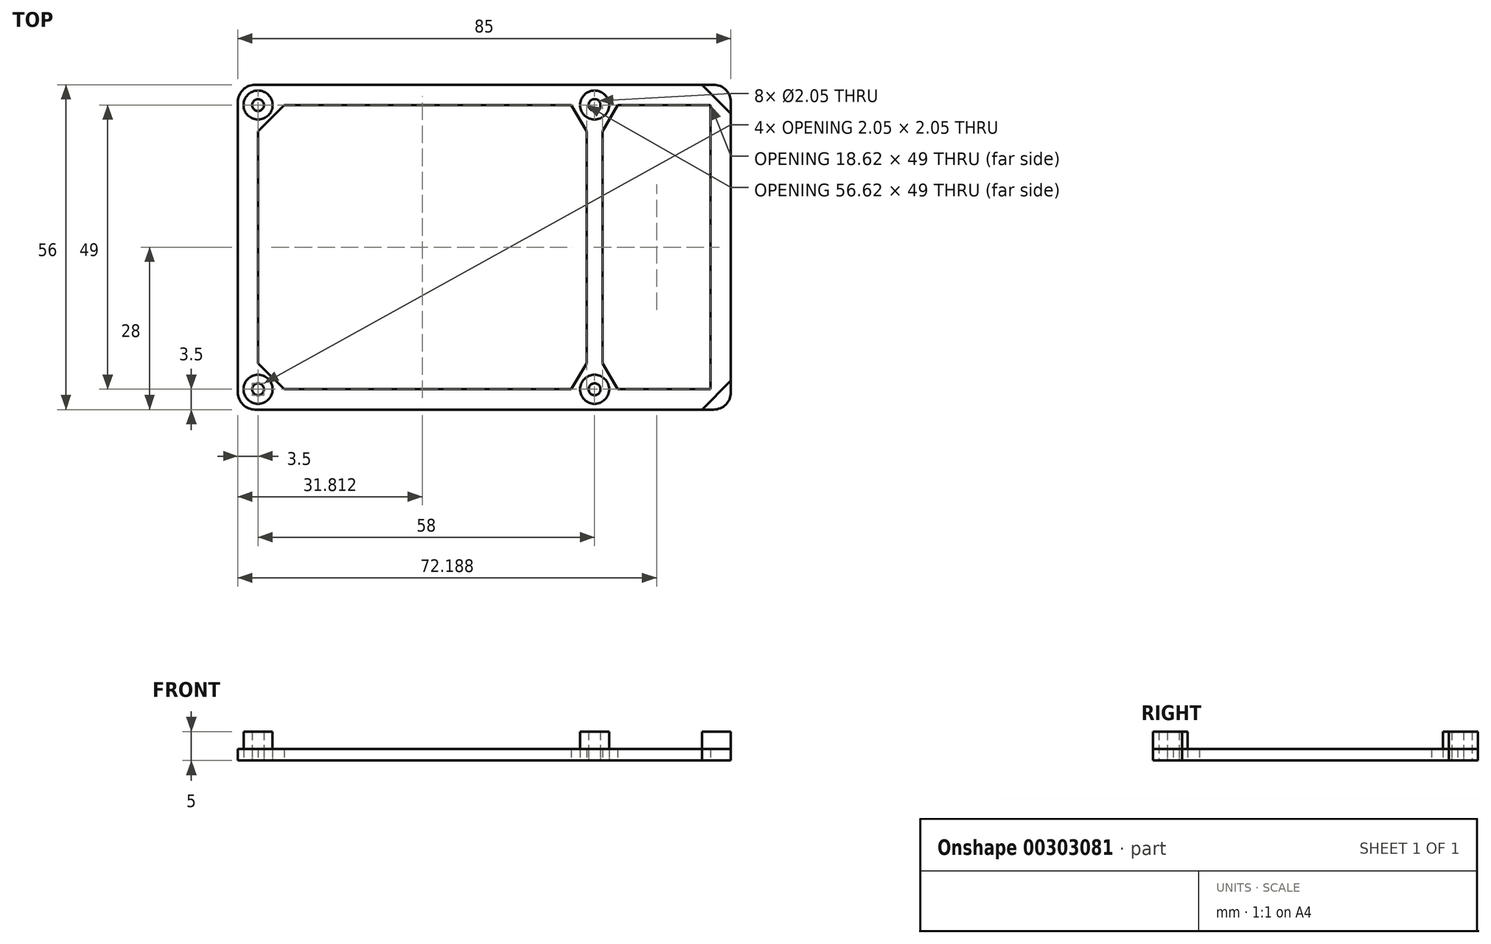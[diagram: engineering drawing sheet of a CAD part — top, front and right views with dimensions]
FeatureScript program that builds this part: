
annotation { "Feature Type Name" : "Feature", "Feature Type Description" : "" }
export const myFeature = defineFeature(function(context is Context, id is Id, definition is map)
    precondition{}
    {
        {
            var Q0;
            Q0=qCreatedBy(makeId("Top.planeOp"),FACE);
            var sketch = newSketch(context, id + "F0", { "sketchPlane" : qUnion([Q0])});
            skLineSegment(sketch, "E0.bottom", {"start": v(-42.5, 28) * mm, "end": v(42.5, 28) * mm});
            skLineSegment(sketch, "E0.top", {"start": v(-42.5, -28) * mm, "end": v(42.5, -28) * mm});
            skLineSegment(sketch, "E0.left", {"start": v(-42.5, 28) * mm, "end": v(-42.5, -28) * mm});
            skLineSegment(sketch, "E0.right", {"start": v(42.5, 28) * mm, "end": v(42.5, -28) * mm});
            skPoint(sketch, "E0.middle", {"position": v(0, 0) * mm});
            skPoint(sketch, "E1", {"position": v(-39, -24.5) * mm});
            skPoint(sketch, "E2", {"position": v(-39, 24.5) * mm});
            skPoint(sketch, "E3", {"position": v(19, 24.5) * mm});
            skPoint(sketch, "E4", {"position": v(19, -24.5) * mm});
            skSolve(sketch);
        }
        {
            var Q0;
            Q0=makeQuery(id+"F0.imprint","IMPRINT",FACE,{"disambiguationData":[TD([[makeQuery(id+"F0.imprint","IMPRINT",EDGE,{"derivedFrom":sQuery(id+"F0.wireOp",EDGE,"E0.bottom")}),-1.0]])]});
            extrude(context, id + "F1", {"entities" : qUnion([Q0]), "depth" : 2 * mm});
        }
        {
            var Q0;
            Q0=makeQuery(id+"F1.opExtrude","SWEPT_EDGE",EDGE,{"disambiguationData":[OSD([sQuery(id+"F0.wireOp",EDGE,"E0.top"),sQuery(id+"F0.wireOp",EDGE,"E0.left")])]});
            var Q1;
            Q1=makeQuery(id+"F1.opExtrude","SWEPT_EDGE",EDGE,{"disambiguationData":[OSD([sQuery(id+"F0.wireOp",EDGE,"E0.bottom"),sQuery(id+"F0.wireOp",EDGE,"E0.left")])]});
            var Q2;
            Q2=makeQuery(id+"F1.opExtrude","SWEPT_EDGE",EDGE,{"disambiguationData":[OSD([sQuery(id+"F0.wireOp",EDGE,"E0.top"),sQuery(id+"F0.wireOp",EDGE,"E0.right")])]});
            var Q3;
            Q3=makeQuery(id+"F1.opExtrude","SWEPT_EDGE",EDGE,{"disambiguationData":[OSD([sQuery(id+"F0.wireOp",EDGE,"E0.bottom"),sQuery(id+"F0.wireOp",EDGE,"E0.right")])]});
            fillet(context, id + "F2", {"entities" : qUnion([Q0, Q1, Q2, Q3]), "radius" : 3 * mm, "tangentPropagation" : true, "allowEdgeOverflow" : false});
        }
        {
            var Q0;
            Q0=qCreatedBy(makeId("Top.planeOp"),FACE);
            var sketch = newSketch(context, id + "F3", { "sketchPlane" : qUnion([Q0])});
            skCircle(sketch, "E5", {"center": v(-39, -24.5) * mm, "radius": 2.5 * mm});
            skCircle(sketch, "E6", {"center": v(-39, 24.5) * mm, "radius": 2.5 * mm});
            skCircle(sketch, "E7", {"center": v(19, -24.5) * mm, "radius": 2.5 * mm});
            skCircle(sketch, "E8", {"center": v(19, 24.5) * mm, "radius": 2.5 * mm});
            skLineSegment(sketch, "E9", {"start": v(42.5, -28) * mm, "end": v(42.5, -23) * mm});
            skLineSegment(sketch, "E10", {"start": v(42.5, -23) * mm, "end": v(37.5, -28) * mm});
            skLineSegment(sketch, "E11", {"start": v(37.5, -28) * mm, "end": v(42.5, -28) * mm});
            skLineSegment(sketch, "E12", {"start": v(42.5, 28) * mm, "end": v(42.5, 23) * mm});
            skLineSegment(sketch, "E13", {"start": v(42.5, 23) * mm, "end": v(37.5, 28) * mm});
            skLineSegment(sketch, "E14", {"start": v(37.5, 28) * mm, "end": v(42.5, 28) * mm});
            skSolve(sketch);
        }
        {
            var Q0;
            Q0 = qSketchRegion(id + "F3", true);
            var Q1;
            Q1=sQuery(id+"F6.wireOp",EDGE,"41c00415-b5be-4618-b273-1da4f6d4129d");
            var Q2;
            Q2=sQuery(id+"F6.wireOp",EDGE,"12e960b8-c61e-41b5-a317-757bdfac7c1a");
            var Q3;
            Q3=sQuery(id+"F6.wireOp",EDGE,"d7424abe-d45f-47b7-acd0-ba5ed3035326");
            extrude(context, id + "F4", {"entities" : qUnion([Q0]), "surfaceEntities" : qUnion([Q1, Q2, Q3]), "depth" : 5 * mm});
        }
        {
            var Q0;
            Q0=sQuery(id+"F0.wireOp",VERTEX,"E2");
            var Q1;
            Q1=sQuery(id+"F0.wireOp",VERTEX,"E3");
            var Q2;
            Q2=sQuery(id+"F0.wireOp",VERTEX,"E4");
            var Q3;
            Q3=sQuery(id+"F0.wireOp",VERTEX,"E1");
            var Q4;
            Q4=makeQuery(id+"F1.opExtrude","SWEPT_BODY",BODY,{"disambiguationData":[OSD([sQuery(id+"F0.wireOp",EDGE,"E0.bottom"),sQuery(id+"F0.wireOp",EDGE,"E0.top"),sQuery(id+"F0.wireOp",EDGE,"E0.left"),sQuery(id+"F0.wireOp",EDGE,"E0.right")])]});
            var Q5;
            Q5=makeQuery(id+"F4.opExtrude","SWEPT_BODY",BODY,{"disambiguationData":[OSD([sQuery(id+"F3.wireOp",EDGE,"E5")])]});
            var Q6;
            Q6=makeQuery(id+"F4.opExtrude","SWEPT_BODY",BODY,{"disambiguationData":[OSD([sQuery(id+"F3.wireOp",EDGE,"E6")])]});
            var Q7;
            Q7=makeQuery(id+"F4.opExtrude","SWEPT_BODY",BODY,{"disambiguationData":[OSD([sQuery(id+"F3.wireOp",EDGE,"E7")])]});
            var Q8;
            Q8=makeQuery(id+"F4.opExtrude","SWEPT_BODY",BODY,{"disambiguationData":[OSD([sQuery(id+"F3.wireOp",EDGE,"E8")])]});
            hole(context, id + "F5", {"style" : HoleStyle.SIMPLE, "endStyle" : HoleEndStyle.BLIND, "oppositeDirection" : true, "holeDiameter" : 2.05 * mm, "holeDepth" : 10 * mm, "tappedDepth" : 12 * mm, "tapClearance" : 3, "locations" : qUnion([Q0, Q1, Q2, Q3]), "scope" : qUnion([Q4, Q5, Q6, Q7, Q8])});
        }
        {
            var Q0;
            Q0=makeQuery(id+"F0.imprint","IMPRINT",FACE,{"disambiguationData":[TD([[makeQuery(id+"F0.imprint","IMPRINT",EDGE,{"derivedFrom":sQuery(id+"F0.wireOp",EDGE,"E0.bottom")}),-1.0]])]});
            var sketch = newSketch(context, id + "F6", { "sketchPlane" : qUnion([Q0])});
            skLineSegment(sketch, "E15", {"start": v(-39, 20) * mm, "end": v(-39, -20) * mm});
            skLineSegment(sketch, "E16", {"start": v(-39, -20) * mm, "end": v(-34.5, -24.5) * mm});
            skLineSegment(sketch, "E17", {"start": v(-34.5, -24.5) * mm, "end": v(15, -24.5) * mm});
            skLineSegment(sketch, "E18", {"start": v(15, -24.5) * mm, "end": v(17.63, -20) * mm});
            skLineSegment(sketch, "E19", {"start": v(17.62, -20) * mm, "end": v(17.62, 20) * mm});
            skLineSegment(sketch, "E20", {"start": v(17.62, 20) * mm, "end": v(15, 24.5) * mm});
            skLineSegment(sketch, "E21", {"start": v(15, 24.5) * mm, "end": v(-34.5, 24.5) * mm});
            skLineSegment(sketch, "E22", {"start": v(-34.5, 24.5) * mm, "end": v(-39, 20) * mm});
            skLineSegment(sketch, "E23", {"start": v(20.38, 20) * mm, "end": v(23, 24.5) * mm});
            skLineSegment(sketch, "E24", {"start": v(23, 24.5) * mm, "end": v(39, 24.5) * mm});
            skLineSegment(sketch, "E25", {"start": v(39, 24.5) * mm, "end": v(39, -24.5) * mm});
            skLineSegment(sketch, "E26", {"start": v(39, -24.5) * mm, "end": v(23, -24.5) * mm});
            skLineSegment(sketch, "E27", {"start": v(23, -24.5) * mm, "end": v(20.37, -20) * mm});
            skLineSegment(sketch, "E28", {"start": v(20.38, -20) * mm, "end": v(20.38, 20) * mm});
            skSolve(sketch);
        }
        {
            var Q0;
            Q0=makeQuery(id+"F6.imprint","IMPRINT",FACE,{"disambiguationData":[TD([[makeQuery(id+"F6.imprint","IMPRINT",EDGE,{"derivedFrom":sQuery(id+"F6.wireOp",EDGE,"E15")}),1.0]])]});
            var Q1;
            Q1=makeQuery(id+"F6.imprint","IMPRINT",FACE,{"disambiguationData":[TD([[makeQuery(id+"F6.imprint","IMPRINT",EDGE,{"derivedFrom":sQuery(id+"F6.wireOp",EDGE,"E23")}),-1.0]])]});
            extrude(context, id + "F7", {"entities" : qUnion([Q0, Q1]), "operationType" : NewBodyOperationType.REMOVE, "depth" : 3 * mm});
        }
        {
            var Q0;
            Q0=makeQuery(id+"F4.opExtrude","SWEPT_EDGE",EDGE,{"disambiguationData":[OSD([sQuery(id+"F3.wireOp",EDGE,"E12"),sQuery(id+"F3.wireOp",EDGE,"E14")])]});
            var Q1;
            Q1=makeQuery(id+"F4.opExtrude","SWEPT_EDGE",EDGE,{"disambiguationData":[OSD([sQuery(id+"F3.wireOp",EDGE,"E9"),sQuery(id+"F3.wireOp",EDGE,"E11")])]});
            fillet(context, id + "F8", {"entities" : qUnion([Q0, Q1]), "radius" : 3 * mm, "tangentPropagation" : true, "allowEdgeOverflow" : false});
        }
    });
